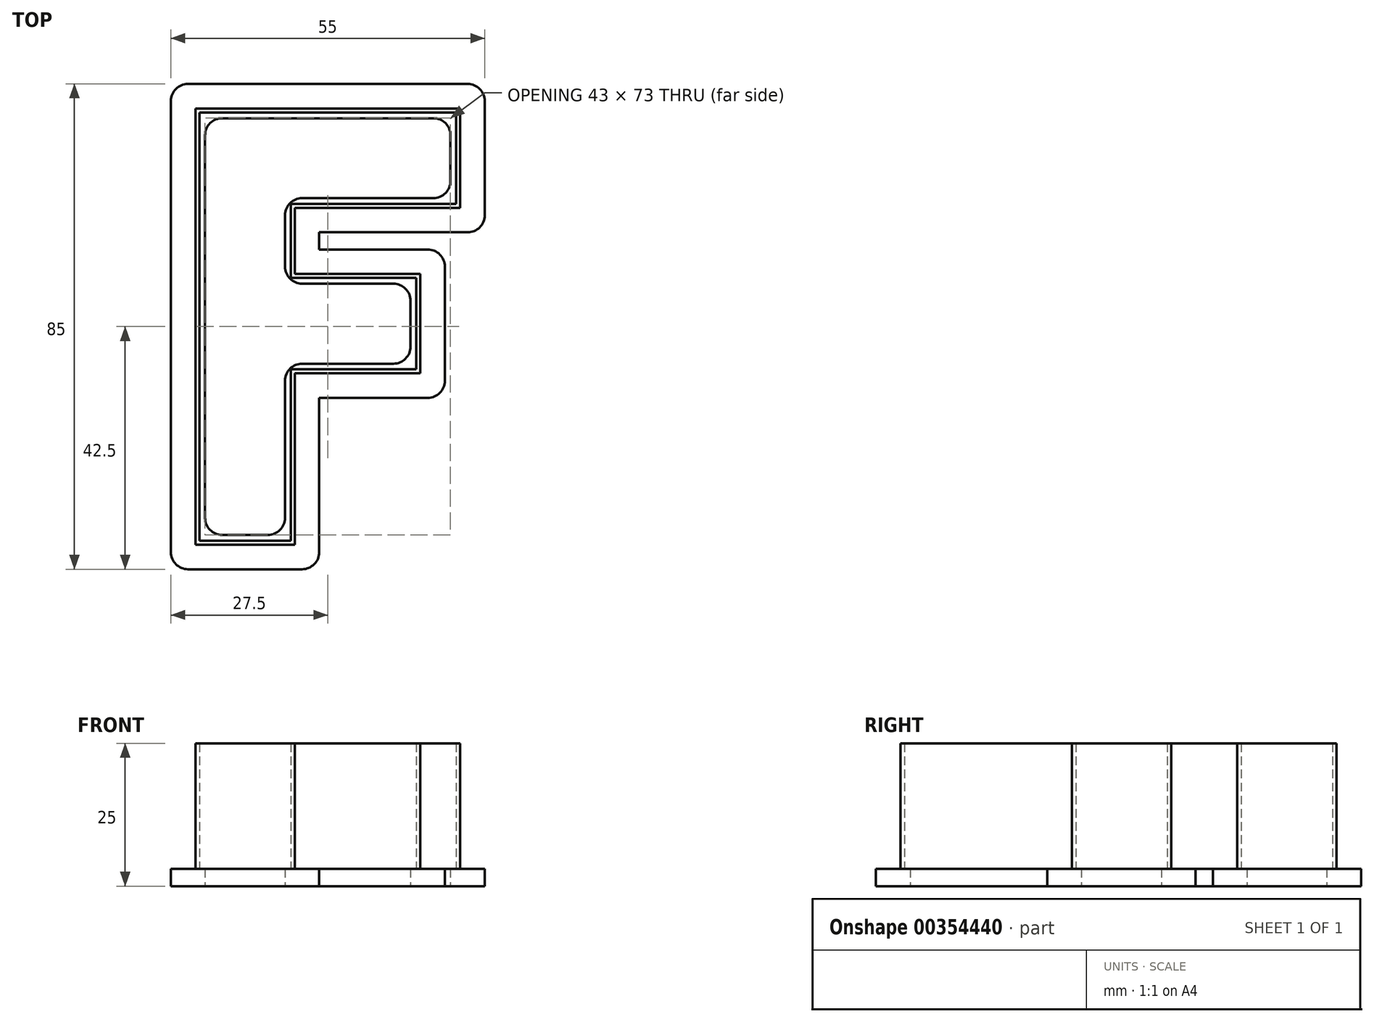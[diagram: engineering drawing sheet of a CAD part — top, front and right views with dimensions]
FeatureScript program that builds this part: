
annotation { "Feature Type Name" : "Feature", "Feature Type Description" : "" }
export const myFeature = defineFeature(function(context is Context, id is Id, definition is map)
    precondition{}
    {
        {
            var Q0;
            Q0=qCreatedBy(makeId("Top.planeOp"),FACE);
            var sketch = newSketch(context, id + "F0", { "sketchPlane" : qUnion([Q0])});
            skLineSegment(sketch, "E0", {"start": v(0, 0) * mm, "end": v(22, 0) * mm});
            skLineSegment(sketch, "E1", {"start": v(22, 0) * mm, "end": v(22, 16) * mm});
            skLineSegment(sketch, "E2", {"start": v(22, 16) * mm, "end": v(0, 16) * mm});
            skLineSegment(sketch, "E3", {"start": v(0, 16) * mm, "end": v(0, 29) * mm});
            skLineSegment(sketch, "E4", {"start": v(0, 29) * mm, "end": v(29, 29) * mm});
            skLineSegment(sketch, "E5", {"start": v(29, 29) * mm, "end": v(29, 45) * mm});
            skLineSegment(sketch, "E6", {"start": v(29, 45) * mm, "end": v(-16, 45) * mm});
            skLineSegment(sketch, "E7", {"start": v(-16, 45) * mm, "end": v(-16, -30) * mm});
            skLineSegment(sketch, "E8", {"start": v(-16, -30) * mm, "end": v(0, -30) * mm});
            skLineSegment(sketch, "E9", {"start": v(0, -30) * mm, "end": v(0, 0) * mm});
            skLineSegment(sketch, "E10.0", {"start": v(5, -35) * mm, "end": v(5, -5) * mm});
            skLineSegment(sketch, "E10.1", {"start": v(-21, -35) * mm, "end": v(5, -35) * mm});
            skLineSegment(sketch, "E10.2", {"start": v(5, -5) * mm, "end": v(27, -5) * mm});
            skLineSegment(sketch, "E10.3", {"start": v(-21, 50) * mm, "end": v(-21, -35) * mm});
            skLineSegment(sketch, "E10.4", {"start": v(34, 50) * mm, "end": v(-21, 50) * mm});
            skLineSegment(sketch, "E10.5", {"start": v(34, 24) * mm, "end": v(34, 50) * mm});
            skLineSegment(sketch, "E10.6", {"start": v(27, -5) * mm, "end": v(27, 21) * mm});
            skLineSegment(sketch, "E10.7", {"start": v(27, 21) * mm, "end": v(5, 21) * mm});
            skLineSegment(sketch, "E10.8", {"start": v(5, 21) * mm, "end": v(5, 24) * mm});
            skLineSegment(sketch, "E10.9", {"start": v(5, 24) * mm, "end": v(34, 24) * mm});
            skLineSegment(sketch, "E11.0", {"start": v(29.7, 45.7) * mm, "end": v(-16.7, 45.7) * mm});
            skLineSegment(sketch, "E11.1", {"start": v(29.7, 28.3) * mm, "end": v(29.7, 45.7) * mm});
            skLineSegment(sketch, "E11.2", {"start": v(-16.7, 45.7) * mm, "end": v(-16.7, -30.7) * mm});
            skLineSegment(sketch, "E11.3", {"start": v(0.7, 28.3) * mm, "end": v(29.7, 28.3) * mm});
            skLineSegment(sketch, "E11.4", {"start": v(0.7, 16.7) * mm, "end": v(0.7, 28.3) * mm});
            skLineSegment(sketch, "E11.5", {"start": v(22.7, 16.7) * mm, "end": v(0.7, 16.7) * mm});
            skLineSegment(sketch, "E11.6", {"start": v(-16.7, -30.7) * mm, "end": v(0.7, -30.7) * mm});
            skLineSegment(sketch, "E11.7", {"start": v(0.7, -30.7) * mm, "end": v(0.7, -0.7) * mm});
            skLineSegment(sketch, "E11.8", {"start": v(0.7, -0.7) * mm, "end": v(22.7, -0.7) * mm});
            skLineSegment(sketch, "E11.9", {"start": v(22.7, -0.7) * mm, "end": v(22.7, 16.7) * mm});
            skLineSegment(sketch, "E12.0", {"start": v(-1, 1) * mm, "end": v(21, 1) * mm});
            skLineSegment(sketch, "E12.1", {"start": v(-1, -29) * mm, "end": v(-1, 1) * mm});
            skLineSegment(sketch, "E12.2", {"start": v(-15, -29) * mm, "end": v(-1, -29) * mm});
            skLineSegment(sketch, "E12.3", {"start": v(-15, 44) * mm, "end": v(-15, -29) * mm});
            skLineSegment(sketch, "E12.4", {"start": v(28, 44) * mm, "end": v(-15, 44) * mm});
            skLineSegment(sketch, "E12.5", {"start": v(21, 15) * mm, "end": v(-1, 15) * mm});
            skLineSegment(sketch, "E12.6", {"start": v(-1, 15) * mm, "end": v(-1, 30) * mm});
            skLineSegment(sketch, "E12.7", {"start": v(-1, 30) * mm, "end": v(28, 30) * mm});
            skLineSegment(sketch, "E12.8", {"start": v(28, 30) * mm, "end": v(28, 44) * mm});
            skLineSegment(sketch, "E13", {"start": v(21, 1) * mm, "end": v(21, 15) * mm});
            skSolve(sketch);
        }
        {
            var Q0;
            Q0=makeQuery(id+"F0.imprint","IMPRINT",FACE,{"disambiguationData":[TD([[makeQuery(id+"F0.imprint","IMPRINT",EDGE,{"derivedFrom":sQuery(id+"F0.wireOp",EDGE,"E10.0")}),1.0]])]});
            var Q1;
            Q1=makeQuery(id+"F0.imprint","IMPRINT",FACE,{"disambiguationData":[TD([[makeQuery(id+"F0.imprint","IMPRINT",EDGE,{"derivedFrom":sQuery(id+"F0.wireOp",EDGE,"E0")}),1.0]])]});
            var Q2;
            Q2=makeQuery(id+"F0.imprint","IMPRINT",FACE,{"disambiguationData":[TD([[makeQuery(id+"F0.imprint","IMPRINT",EDGE,{"derivedFrom":sQuery(id+"F0.wireOp",EDGE,"E0")}),-1.0]])]});
            extrude(context, id + "F1", {"entities" : qUnion([Q0, Q1, Q2]), "depth" : 3 * mm});
        }
        {
            var Q0;
            Q0=makeQuery(id+"F0.imprint","IMPRINT",FACE,{"disambiguationData":[TD([[makeQuery(id+"F0.imprint","IMPRINT",EDGE,{"derivedFrom":sQuery(id+"F0.wireOp",EDGE,"E0")}),-1.0]])]});
            extrude(context, id + "F2", {"entities" : qUnion([Q0]), "operationType" : NewBodyOperationType.ADD, "depth" : 25 * mm});
        }
        {
            var Q0;
            Q0=makeQuery(id+"F1.opExtrude","SWEPT_EDGE",EDGE,{"disambiguationData":[OSD([sQuery(id+"F0.wireOp",EDGE,"E10.6"),sQuery(id+"F0.wireOp",EDGE,"E10.7")])]});
            var Q1;
            Q1=makeQuery(id+"F1.opExtrude","SWEPT_EDGE",EDGE,{"disambiguationData":[OSD([sQuery(id+"F0.wireOp",EDGE,"E12.5"),sQuery(id+"F0.wireOp",EDGE,"E12.6")])]});
            var Q2;
            Q2=makeQuery(id+"F1.opExtrude","SWEPT_EDGE",EDGE,{"disambiguationData":[OSD([sQuery(id+"F0.wireOp",EDGE,"E10.2"),sQuery(id+"F0.wireOp",EDGE,"E10.6")])]});
            var Q3;
            Q3=makeQuery(id+"F1.opExtrude","SWEPT_EDGE",EDGE,{"disambiguationData":[OSD([sQuery(id+"F0.wireOp",EDGE,"E10.0"),sQuery(id+"F0.wireOp",EDGE,"E10.1")])]});
            var Q4;
            Q4=makeQuery(id+"F1.opExtrude","SWEPT_EDGE",EDGE,{"disambiguationData":[OSD([sQuery(id+"F0.wireOp",EDGE,"E10.1"),sQuery(id+"F0.wireOp",EDGE,"E10.3")])]});
            var Q5;
            Q5=makeQuery(id+"F1.opExtrude","SWEPT_EDGE",EDGE,{"disambiguationData":[OSD([sQuery(id+"F0.wireOp",EDGE,"E10.3"),sQuery(id+"F0.wireOp",EDGE,"E10.4")])]});
            var Q6;
            Q6=makeQuery(id+"F1.opExtrude","SWEPT_EDGE",EDGE,{"disambiguationData":[OSD([sQuery(id+"F0.wireOp",EDGE,"E10.5"),sQuery(id+"F0.wireOp",EDGE,"E10.9")])]});
            var Q7;
            Q7=makeQuery(id+"F1.opExtrude","SWEPT_EDGE",EDGE,{"disambiguationData":[OSD([sQuery(id+"F0.wireOp",EDGE,"E10.4"),sQuery(id+"F0.wireOp",EDGE,"E10.5")])]});
            var Q8;
            Q8=makeQuery(id+"F1.opExtrude","SWEPT_EDGE",EDGE,{"disambiguationData":[OSD([sQuery(id+"F0.wireOp",EDGE,"E12.6"),sQuery(id+"F0.wireOp",EDGE,"E12.7")])]});
            var Q9;
            Q9=makeQuery(id+"F1.opExtrude","SWEPT_EDGE",EDGE,{"disambiguationData":[OSD([sQuery(id+"F0.wireOp",EDGE,"E12.0"),sQuery(id+"F0.wireOp",EDGE,"E12.1")])]});
            var Q10;
            Q10=makeQuery(id+"F1.opExtrude","SWEPT_EDGE",EDGE,{"disambiguationData":[OSD([sQuery(id+"F0.wireOp",EDGE,"E12.1"),sQuery(id+"F0.wireOp",EDGE,"E12.2")])]});
            var Q11;
            Q11=makeQuery(id+"F1.opExtrude","SWEPT_EDGE",EDGE,{"disambiguationData":[OSD([sQuery(id+"F0.wireOp",EDGE,"E12.2"),sQuery(id+"F0.wireOp",EDGE,"E12.3")])]});
            var Q12;
            Q12=makeQuery(id+"F1.opExtrude","SWEPT_EDGE",EDGE,{"disambiguationData":[OSD([sQuery(id+"F0.wireOp",EDGE,"E12.0"),sQuery(id+"F0.wireOp",EDGE,"E13")])]});
            var Q13;
            Q13=makeQuery(id+"F1.opExtrude","SWEPT_EDGE",EDGE,{"disambiguationData":[OSD([sQuery(id+"F0.wireOp",EDGE,"E12.5"),sQuery(id+"F0.wireOp",EDGE,"E13")])]});
            var Q14;
            Q14=makeQuery(id+"F1.opExtrude","SWEPT_EDGE",EDGE,{"disambiguationData":[OSD([sQuery(id+"F0.wireOp",EDGE,"E12.7"),sQuery(id+"F0.wireOp",EDGE,"E12.8")])]});
            var Q15;
            Q15=makeQuery(id+"F1.opExtrude","SWEPT_EDGE",EDGE,{"disambiguationData":[OSD([sQuery(id+"F0.wireOp",EDGE,"E12.4"),sQuery(id+"F0.wireOp",EDGE,"E12.8")])]});
            var Q16;
            Q16=makeQuery(id+"F1.opExtrude","SWEPT_EDGE",EDGE,{"disambiguationData":[OSD([sQuery(id+"F0.wireOp",EDGE,"E12.3"),sQuery(id+"F0.wireOp",EDGE,"E12.4")])]});
            fillet(context, id + "F3", {"entities" : qUnion([Q0, Q1, Q2, Q3, Q4, Q5, Q6, Q7, Q8, Q9, Q10, Q11, Q12, Q13, Q14, Q15, Q16]), "radius" : 3 * mm, "tangentPropagation" : true, "allowEdgeOverflow" : false});
        }
    });
